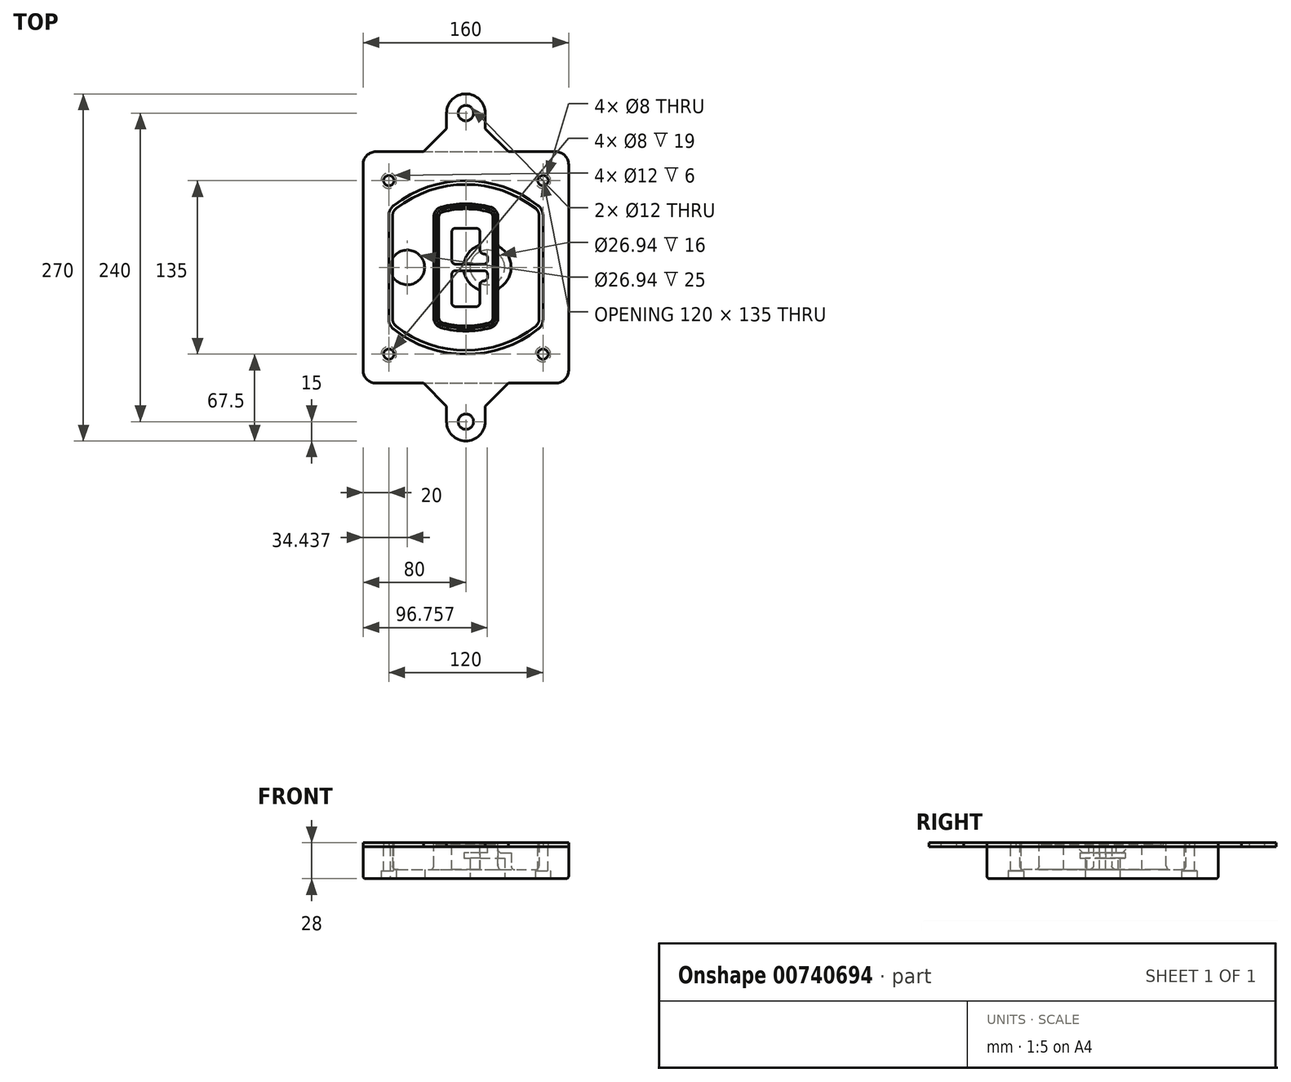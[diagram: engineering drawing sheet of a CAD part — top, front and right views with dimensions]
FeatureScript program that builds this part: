
annotation { "Feature Type Name" : "Feature", "Feature Type Description" : "" }
export const myFeature = defineFeature(function(context is Context, id is Id, definition is map)
    precondition{}
    {
        {
            var Q0;
            Q0=qCreatedBy(makeId("Top.planeOp"),FACE);
            var sketch = newSketch(context, id + "F0", { "sketchPlane" : qUnion([Q0])});
            skPoint(sketch, "E0.rect.middle", {"position": v(0, 0) * mm});
            skLineSegment(sketch, "E1.bottom", {"start": v(-70, -90) * mm, "end": v(70, -90) * mm});
            skLineSegment(sketch, "E1.top", {"start": v(-70, 90) * mm, "end": v(70, 90) * mm});
            skLineSegment(sketch, "E1.left", {"start": v(-80, -80) * mm, "end": v(-80, 80) * mm});
            skLineSegment(sketch, "E1.right", {"start": v(80, -80) * mm, "end": v(80, 80) * mm});
            skLineSegment(sketch, "E2", {"start": v(-80, 90) * mm, "end": v(80, -90) * mm, "construction": true});
            skLineSegment(sketch, "E3", {"start": v(80, 90) * mm, "end": v(-80, -90) * mm, "construction": true});
            skCircle(sketch, "E4", {"center": v(-60, 67.5) * mm, "radius": 4 * mm});
            skCircle(sketch, "E5", {"center": v(60, 67.5) * mm, "radius": 4 * mm});
            skCircle(sketch, "E6", {"center": v(60, -67.5) * mm, "radius": 4 * mm});
            skCircle(sketch, "E7", {"center": v(-60, -67.5) * mm, "radius": 4 * mm});
            skLineSegment(sketch, "E8", {"start": v(-60, 67.5) * mm, "end": v(60, 67.5) * mm, "construction": true});
            skLineSegment(sketch, "E9", {"start": v(60, 67.5) * mm, "end": v(60, -67.5) * mm, "construction": true});
            skLineSegment(sketch, "E10", {"start": v(60, -67.5) * mm, "end": v(-60, -67.5) * mm, "construction": true});
            skLineSegment(sketch, "E11", {"start": v(-60, -67.5) * mm, "end": v(-60, 67.5) * mm, "construction": true});
            skLineSegment(sketch, "E12", {"start": v(-60, 40.3) * mm, "end": v(-60, -40.3) * mm});
            skLineSegment(sketch, "E13", {"start": v(60, 40.3) * mm, "end": v(60, -40.3) * mm});
            skArc(sketch, "E14", {"start": v(56.15, 48.18) * mm, "mid": v(0, 67.5) * mm, "end": v(-56.15, 48.18) * mm});
            skArc(sketch, "E15", {"start": v(-56.15, -48.18) * mm, "mid": v(0, -67.5) * mm, "end": v(56.15, -48.18) * mm});
            skLineSegment(sketch, "E16", {"start": v(-60, 0) * mm, "end": v(60, 0) * mm, "construction": true});
            skPoint(sketch, "E17.visualSharp", {"position": v(-60, -45) * mm});
            skArc(sketch, "E17.filletArc", {"start": v(-60, -40.3) * mm, "mid": v(-58.99, -44.68) * mm, "end": v(-56.15, -48.18) * mm});
            skPoint(sketch, "E18.visualSharp", {"position": v(-60, 45) * mm});
            skArc(sketch, "E18.filletArc", {"start": v(-56.15, 48.18) * mm, "mid": v(-58.99, 44.68) * mm, "end": v(-60, 40.3) * mm});
            skPoint(sketch, "E19.visualSharp", {"position": v(60, 45) * mm});
            skArc(sketch, "E19.filletArc", {"start": v(60, 40.3) * mm, "mid": v(58.99, 44.68) * mm, "end": v(56.15, 48.18) * mm});
            skPoint(sketch, "E20.visualSharp", {"position": v(60, -45) * mm});
            skArc(sketch, "E20.filletArc", {"start": v(56.15, -48.18) * mm, "mid": v(58.99, -44.68) * mm, "end": v(60, -40.3) * mm});
            skPoint(sketch, "E21.visualSharp", {"position": v(-80, 90) * mm});
            skArc(sketch, "E21.filletArc", {"start": v(-70, 90) * mm, "mid": v(-77.07, 87.07) * mm, "end": v(-80, 80) * mm});
            skPoint(sketch, "E22.visualSharp", {"position": v(80, 90) * mm});
            skArc(sketch, "E22.filletArc", {"start": v(80, 80) * mm, "mid": v(77.07, 87.07) * mm, "end": v(70, 90) * mm});
            skPoint(sketch, "E23.visualSharp", {"position": v(80, -90) * mm});
            skArc(sketch, "E23.filletArc", {"start": v(70, -90) * mm, "mid": v(77.07, -87.07) * mm, "end": v(80, -80) * mm});
            skPoint(sketch, "E24.visualSharp", {"position": v(-80, -90) * mm});
            skArc(sketch, "E24.filletArc", {"start": v(-80, -80) * mm, "mid": v(-77.07, -87.07) * mm, "end": v(-70, -90) * mm});
            skArc(sketch, "E25.0", {"start": v(57, 40.3) * mm, "mid": v(56.3, 43.36) * mm, "end": v(54.3, 45.81) * mm});
            skLineSegment(sketch, "E25.1", {"start": v(57, 40.3) * mm, "end": v(57, -40.3) * mm});
            skArc(sketch, "E25.2", {"start": v(54.3, -45.81) * mm, "mid": v(56.3, -43.36) * mm, "end": v(57, -40.3) * mm});
            skArc(sketch, "E25.3", {"start": v(-54.3, -45.81) * mm, "mid": v(0, -64.5) * mm, "end": v(54.3, -45.81) * mm});
            skArc(sketch, "E25.4", {"start": v(-57, -40.3) * mm, "mid": v(-56.3, -43.36) * mm, "end": v(-54.3, -45.81) * mm});
            skArc(sketch, "E25.5", {"start": v(54.3, 45.81) * mm, "mid": v(0, 64.5) * mm, "end": v(-54.3, 45.81) * mm});
            skLineSegment(sketch, "E25.6", {"start": v(-57, 40.3) * mm, "end": v(-57, -40.3) * mm});
            skArc(sketch, "E25.7", {"start": v(-54.3, 45.81) * mm, "mid": v(-56.3, 43.36) * mm, "end": v(-57, 40.3) * mm});
            skArc(sketch, "E26.0", {"start": v(-58.62, 51.33) * mm, "mid": v(-62.58, 46.43) * mm, "end": v(-64, 40.3) * mm});
            skArc(sketch, "E26.1", {"start": v(58.62, 51.33) * mm, "mid": v(0, 71.5) * mm, "end": v(-58.62, 51.33) * mm});
            skArc(sketch, "E26.2", {"start": v(64, 40.3) * mm, "mid": v(62.58, 46.43) * mm, "end": v(58.62, 51.33) * mm});
            skLineSegment(sketch, "E26.3", {"start": v(64, 40.3) * mm, "end": v(64, -40.3) * mm});
            skArc(sketch, "E26.4", {"start": v(58.62, -51.33) * mm, "mid": v(62.58, -46.43) * mm, "end": v(64, -40.3) * mm});
            skLineSegment(sketch, "E26.5", {"start": v(-64, 40.3) * mm, "end": v(-64, -40.3) * mm});
            skArc(sketch, "E26.6", {"start": v(-58.62, -51.33) * mm, "mid": v(0, -71.5) * mm, "end": v(58.62, -51.33) * mm});
            skArc(sketch, "E26.7", {"start": v(-64, -40.3) * mm, "mid": v(-62.58, -46.43) * mm, "end": v(-58.62, -51.33) * mm});
            skSolve(sketch);
        }
        {
            var Q0;
            Q0=makeQuery(id+"F0.imprint","IMPRINT",FACE,{"disambiguationData":[TD([[makeQuery(id+"F0.imprint","IMPRINT",EDGE,{"derivedFrom":sQuery(id+"F0.wireOp",EDGE,"E1.bottom")}),1.0]])]});
            var Q1;
            Q1=makeQuery(id+"F0.imprint","IMPRINT",FACE,{"disambiguationData":[TD([[makeQuery(id+"F0.imprint","IMPRINT",EDGE,{"derivedFrom":sQuery(id+"F0.wireOp",EDGE,"E12")}),1.0]])]});
            var Q2;
            Q2=makeQuery(id+"F0.imprint","IMPRINT",FACE,{"disambiguationData":[TD([[makeQuery(id+"F0.imprint","IMPRINT",EDGE,{"derivedFrom":sQuery(id+"F0.wireOp",EDGE,"E25.0")}),1.0]])]});
            var Q3;
            Q3=makeQuery(id+"F0.imprint","IMPRINT",FACE,{"disambiguationData":[TD([[makeQuery(id+"F0.imprint","IMPRINT",EDGE,{"derivedFrom":sQuery(id+"F0.wireOp",EDGE,"E12")}),-1.0]])]});
            extrude(context, id + "F1", {"entities" : qUnion([Q0, Q1, Q2, Q3]), "oppositeDirection" : true, "depth" : 25 * mm});
        }
        {
            var Q0;
            Q0=makeQuery(id+"F0.imprint","IMPRINT",FACE,{"disambiguationData":[TD([[makeQuery(id+"F0.imprint","IMPRINT",EDGE,{"derivedFrom":sQuery(id+"F0.wireOp",EDGE,"E12")}),1.0]])]});
            extrude(context, id + "F2", {"entities" : qUnion([Q0]), "operationType" : NewBodyOperationType.ADD, "depth" : 3 * mm});
        }
        {
            var Q0;
            Q0=makeQuery(id+"F0.imprint","IMPRINT",FACE,{"disambiguationData":[TD([[makeQuery(id+"F0.imprint","IMPRINT",EDGE,{"derivedFrom":sQuery(id+"F0.wireOp",EDGE,"E25.0")}),1.0]])]});
            extrude(context, id + "F3", {"entities" : qUnion([Q0]), "operationType" : NewBodyOperationType.REMOVE, "oppositeDirection" : true, "depth" : 18 * mm});
        }
        {
            var Q0;
            Q0=makeQuery(id+"F2.opExtrude","CAP_FACE",FACE,{"disambiguationData":[OSD([sQuery(id+"F0.wireOp",EDGE,"E12"),sQuery(id+"F0.wireOp",EDGE,"E13"),sQuery(id+"F0.wireOp",EDGE,"E14"),sQuery(id+"F0.wireOp",EDGE,"E15"),sQuery(id+"F0.wireOp",EDGE,"E17.filletArc"),sQuery(id+"F0.wireOp",EDGE,"E18.filletArc"),sQuery(id+"F0.wireOp",EDGE,"E19.filletArc"),sQuery(id+"F0.wireOp",EDGE,"E20.filletArc"),sQuery(id+"F0.wireOp",EDGE,"E25.0"),sQuery(id+"F0.wireOp",EDGE,"E25.1"),sQuery(id+"F0.wireOp",EDGE,"E25.2"),sQuery(id+"F0.wireOp",EDGE,"E25.3"),sQuery(id+"F0.wireOp",EDGE,"E25.4"),sQuery(id+"F0.wireOp",EDGE,"E25.5"),sQuery(id+"F0.wireOp",EDGE,"E25.6"),sQuery(id+"F0.wireOp",EDGE,"E25.7")])],"isStart":false});
            var sketch = newSketch(context, id + "F4", { "sketchPlane" : qUnion([Q0])});
            skArc(sketch, "E27.0", {"start": v(-19.08, -46.97) * mm, "mid": v(0, -49.5) * mm, "end": v(19.08, -46.97) * mm});
            skArc(sketch, "E28.0", {"start": v(19.08, 46.97) * mm, "mid": v(0, 49.5) * mm, "end": v(-19.08, 46.97) * mm});
            skLineSegment(sketch, "E29", {"start": v(-25, 39.25) * mm, "end": v(-25, -39.25) * mm});
            skLineSegment(sketch, "E30", {"start": v(25, 39.25) * mm, "end": v(25, -39.25) * mm});
            skLineSegment(sketch, "E31", {"start": v(-25, 45.1) * mm, "end": v(25, 45.1) * mm, "construction": true});
            skLineSegment(sketch, "E32", {"start": v(-25, -45.1) * mm, "end": v(25, -45.1) * mm, "construction": true});
            skPoint(sketch, "E33.visualSharp", {"position": v(-25, 45.1) * mm});
            skArc(sketch, "E33.filletArc", {"start": v(-19.08, 46.97) * mm, "mid": v(-23.35, 44.11) * mm, "end": v(-25, 39.25) * mm});
            skPoint(sketch, "E34.visualSharp", {"position": v(25, 45.1) * mm});
            skArc(sketch, "E34.filletArc", {"start": v(25, 39.25) * mm, "mid": v(23.35, 44.11) * mm, "end": v(19.08, 46.97) * mm});
            skPoint(sketch, "E35.visualSharp", {"position": v(25, -45.1) * mm});
            skArc(sketch, "E35.filletArc", {"start": v(19.08, -46.97) * mm, "mid": v(23.35, -44.11) * mm, "end": v(25, -39.25) * mm});
            skPoint(sketch, "E36.visualSharp", {"position": v(-25, -45.1) * mm});
            skArc(sketch, "E36.filletArc", {"start": v(-25, -39.25) * mm, "mid": v(-23.35, -44.11) * mm, "end": v(-19.08, -46.97) * mm});
            skArc(sketch, "E37.0", {"start": v(54.3, 45.81) * mm, "mid": v(0, 64.5) * mm, "end": v(-54.3, 45.81) * mm});
            skArc(sketch, "E37.1", {"start": v(-54.3, 45.81) * mm, "mid": v(-56.3, 43.36) * mm, "end": v(-57, 40.3) * mm});
            skLineSegment(sketch, "E37.2", {"start": v(-57, 40.3) * mm, "end": v(-57, -40.3) * mm});
            skArc(sketch, "E37.3", {"start": v(-57, -40.3) * mm, "mid": v(-56.3, -43.36) * mm, "end": v(-54.3, -45.81) * mm});
            skArc(sketch, "E37.4", {"start": v(-54.3, -45.81) * mm, "mid": v(0, -64.5) * mm, "end": v(54.3, -45.81) * mm});
            skArc(sketch, "E37.5", {"start": v(54.3, -45.81) * mm, "mid": v(56.3, -43.36) * mm, "end": v(57, -40.3) * mm});
            skLineSegment(sketch, "E37.6", {"start": v(57, 40.3) * mm, "end": v(57, -40.3) * mm});
            skArc(sketch, "E37.7", {"start": v(57, 40.3) * mm, "mid": v(56.3, 43.36) * mm, "end": v(54.3, 45.81) * mm});
            skLineSegment(sketch, "E38.0", {"start": v(23, 39.25) * mm, "end": v(23, -39.25) * mm});
            skArc(sketch, "E38.1", {"start": v(18.56, -45.04) * mm, "mid": v(21.76, -42.9) * mm, "end": v(23, -39.25) * mm});
            skArc(sketch, "E38.2", {"start": v(-18.56, -45.04) * mm, "mid": v(0, -47.5) * mm, "end": v(18.56, -45.04) * mm});
            skArc(sketch, "E38.3", {"start": v(-23, -39.25) * mm, "mid": v(-21.76, -42.9) * mm, "end": v(-18.56, -45.04) * mm});
            skLineSegment(sketch, "E38.4", {"start": v(-23, 39.25) * mm, "end": v(-23, -39.25) * mm});
            skArc(sketch, "E38.5", {"start": v(23, 39.25) * mm, "mid": v(21.76, 42.9) * mm, "end": v(18.56, 45.04) * mm});
            skArc(sketch, "E38.6", {"start": v(-18.56, 45.04) * mm, "mid": v(-21.76, 42.9) * mm, "end": v(-23, 39.25) * mm});
            skArc(sketch, "E38.7", {"start": v(18.56, 45.04) * mm, "mid": v(0, 47.5) * mm, "end": v(-18.56, 45.04) * mm});
            skArc(sketch, "E39.0", {"start": v(21, 39.25) * mm, "mid": v(20.18, 41.68) * mm, "end": v(18.04, 43.1) * mm});
            skLineSegment(sketch, "E39.1", {"start": v(21, 39.25) * mm, "end": v(21, -39.25) * mm});
            skArc(sketch, "E39.2", {"start": v(18.04, -43.1) * mm, "mid": v(20.18, -41.68) * mm, "end": v(21, -39.25) * mm});
            skArc(sketch, "E39.3", {"start": v(-18.04, -43.1) * mm, "mid": v(0, -45.5) * mm, "end": v(18.04, -43.1) * mm});
            skArc(sketch, "E39.4", {"start": v(-21, -39.25) * mm, "mid": v(-20.18, -41.68) * mm, "end": v(-18.04, -43.1) * mm});
            skArc(sketch, "E39.5", {"start": v(18.04, 43.1) * mm, "mid": v(0, 45.5) * mm, "end": v(-18.04, 43.1) * mm});
            skLineSegment(sketch, "E39.6", {"start": v(-21, 39.25) * mm, "end": v(-21, -39.25) * mm});
            skArc(sketch, "E39.7", {"start": v(-18.04, 43.1) * mm, "mid": v(-20.18, 41.68) * mm, "end": v(-21, 39.25) * mm});
            skLineSegment(sketch, "E40", {"start": v(-25, 0) * mm, "end": v(25, 0) * mm, "construction": true});
            skLineSegment(sketch, "E41", {"start": v(-11, 5.5) * mm, "end": v(-11, 27.5) * mm});
            skLineSegment(sketch, "E42", {"start": v(-8, 30.5) * mm, "end": v(8, 30.5) * mm});
            skLineSegment(sketch, "E43", {"start": v(11, 27.5) * mm, "end": v(11, 13.5) * mm});
            skLineSegment(sketch, "E44", {"start": v(14, 10.5) * mm, "end": v(14, 10.5) * mm});
            skLineSegment(sketch, "E45", {"start": v(17, 7.5) * mm, "end": v(17, 5.5) * mm});
            skLineSegment(sketch, "E46", {"start": v(14, 2.5) * mm, "end": v(-8, 2.5) * mm});
            skPoint(sketch, "E47.visualSharp", {"position": v(-11, 30.5) * mm});
            skArc(sketch, "E47.filletArc", {"start": v(-8, 30.5) * mm, "mid": v(-10.12, 29.62) * mm, "end": v(-11, 27.5) * mm});
            skPoint(sketch, "E48.visualSharp", {"position": v(11, 30.5) * mm});
            skArc(sketch, "E48.filletArc", {"start": v(11, 27.5) * mm, "mid": v(10.12, 29.62) * mm, "end": v(8, 30.5) * mm});
            skPoint(sketch, "E49.visualSharp", {"position": v(11, 10.5) * mm});
            skArc(sketch, "E49.filletArc", {"start": v(11, 13.5) * mm, "mid": v(11.88, 11.38) * mm, "end": v(14, 10.5) * mm});
            skPoint(sketch, "E50.visualSharp", {"position": v(17, 10.5) * mm});
            skArc(sketch, "E50.filletArc", {"start": v(17, 7.5) * mm, "mid": v(16.12, 9.62) * mm, "end": v(14, 10.5) * mm});
            skPoint(sketch, "E51.visualSharp", {"position": v(17, 2.5) * mm});
            skArc(sketch, "E51.filletArc", {"start": v(14, 2.5) * mm, "mid": v(16.12, 3.38) * mm, "end": v(17, 5.5) * mm});
            skPoint(sketch, "E52.visualSharp", {"position": v(-11, 2.5) * mm});
            skArc(sketch, "E52.filletArc", {"start": v(-11, 5.5) * mm, "mid": v(-10.12, 3.38) * mm, "end": v(-8, 2.5) * mm});
            skLineSegment(sketch, "E53.0.MirrorCS", {"start": v(14, -2.5) * mm, "end": v(-8, -2.5) * mm});
            skArc(sketch, "E54.0.MirrorCS", {"start": v(-11, -5.5) * mm, "mid": v(-10.12, -3.38) * mm, "end": v(-8, -2.5) * mm});
            skLineSegment(sketch, "E55.0.MirrorCS", {"start": v(-11, -5.5) * mm, "end": v(-11, -27.5) * mm});
            skArc(sketch, "E56.0.MirrorCS", {"start": v(-8, -30.5) * mm, "mid": v(-10.12, -29.62) * mm, "end": v(-11, -27.5) * mm});
            skLineSegment(sketch, "E57.0.MirrorCS", {"start": v(-8, -30.5) * mm, "end": v(8, -30.5) * mm});
            skArc(sketch, "E58.0.MirrorCS", {"start": v(11, -27.5) * mm, "mid": v(10.12, -29.62) * mm, "end": v(8, -30.5) * mm});
            skLineSegment(sketch, "E59.0.MirrorCS", {"start": v(11, -27.5) * mm, "end": v(11, -13.5) * mm});
            skArc(sketch, "E60.0.MirrorCS", {"start": v(11, -13.5) * mm, "mid": v(11.88, -11.38) * mm, "end": v(14, -10.5) * mm});
            skArc(sketch, "E61.0.MirrorCS", {"start": v(17, -7.5) * mm, "mid": v(16.12, -9.62) * mm, "end": v(14, -10.5) * mm});
            skLineSegment(sketch, "E62.0.MirrorCS", {"start": v(17, -7.5) * mm, "end": v(17, -5.5) * mm});
            skArc(sketch, "E63.0.MirrorCS", {"start": v(14, -2.5) * mm, "mid": v(16.12, -3.38) * mm, "end": v(17, -5.5) * mm});
            skSolve(sketch);
        }
        {
            var Q0;
            Q0=makeQuery(id+"F4.imprint","IMPRINT",FACE,{"disambiguationData":[TD([[makeQuery(id+"F4.imprint","IMPRINT",EDGE,{"derivedFrom":sQuery(id+"F4.wireOp",EDGE,"E27.0")}),1.0]])]});
            var Q1;
            Q1=makeQuery(id+"F4.imprint","IMPRINT",FACE,{"disambiguationData":[TD([[makeQuery(id+"F4.imprint","IMPRINT",EDGE,{"derivedFrom":sQuery(id+"F4.wireOp",EDGE,"E38.0")}),-1.0]])]});
            var Q2;
            Q2=makeQuery(id+"F4.imprint","IMPRINT",FACE,{"disambiguationData":[TD([[makeQuery(id+"F4.imprint","IMPRINT",EDGE,{"derivedFrom":sQuery(id+"F4.wireOp",EDGE,"E39.0")}),1.0]])]});
            extrude(context, id + "F5", {"entities" : qUnion([Q0, Q1, Q2]), "operationType" : NewBodyOperationType.ADD, "endBound" : BoundingType.UP_TO_NEXT, "oppositeDirection" : true, "depth" : 25 * mm});
        }
        {
            var Q0;
            Q0=makeQuery(id+"F4.imprint","IMPRINT",FACE,{"disambiguationData":[TD([[makeQuery(id+"F4.imprint","IMPRINT",EDGE,{"derivedFrom":sQuery(id+"F4.wireOp",EDGE,"E38.0")}),-1.0]])]});
            extrude(context, id + "F6", {"entities" : qUnion([Q0]), "operationType" : NewBodyOperationType.REMOVE, "oppositeDirection" : true, "depth" : 2 * mm});
        }
        {
            var Q0;
            Q0=makeQuery(id+"F1.opExtrude","CAP_FACE",FACE,{"disambiguationData":[OSD([sQuery(id+"F0.wireOp",EDGE,"E1.bottom"),sQuery(id+"F0.wireOp",EDGE,"E1.top"),sQuery(id+"F0.wireOp",EDGE,"E1.left"),sQuery(id+"F0.wireOp",EDGE,"E1.right"),sQuery(id+"F0.wireOp",EDGE,"E4"),sQuery(id+"F0.wireOp",EDGE,"E5"),sQuery(id+"F0.wireOp",EDGE,"E6"),sQuery(id+"F0.wireOp",EDGE,"E7"),sQuery(id+"F0.wireOp",EDGE,"E21.filletArc"),sQuery(id+"F0.wireOp",EDGE,"E22.filletArc"),sQuery(id+"F0.wireOp",EDGE,"E23.filletArc"),sQuery(id+"F0.wireOp",EDGE,"E24.filletArc")])],"isStart":false});
            var sketch = newSketch(context, id + "F7", { "sketchPlane" : qUnion([Q0])});
            skCircle(sketch, "E64", {"center": v(16.76, 0) * mm, "radius": 13.47 * mm});
            skCircle(sketch, "E65", {"center": v(-45.56, 0) * mm, "radius": 13.47 * mm});
            skLineSegment(sketch, "E66", {"start": v(80, 0) * mm, "end": v(-80, 0) * mm});
            skCircle(sketch, "E67", {"center": v(16.76, 0) * mm, "radius": 18.47 * mm});
            skCircle(sketch, "E68", {"center": v(60, -67.5) * mm, "radius": 6 * mm});
            skCircle(sketch, "E69", {"center": v(-60, -67.5) * mm, "radius": 6 * mm});
            skCircle(sketch, "E70", {"center": v(-60, 67.5) * mm, "radius": 6 * mm});
            skCircle(sketch, "E71", {"center": v(60, 67.5) * mm, "radius": 6 * mm});
            skSolve(sketch);
        }
        {
            var Q0;
            {var subQ1=sQuery(id+"F7.wireOp",EDGE,"E66");var subQ4=sQuery(id+"F7.wireOp",EDGE,"E64");var subQ6=makeQuery(id+"F7.imprint","INTERSECT",VERTEX,{"disambiguationData":[OD(0.0)],"derivedFrom":[subQ4,subQ1]});Q0=makeQuery(id+"F7.imprint","IMPRINT",FACE,{"disambiguationData":[TD([[makeQuery(id+"F7.imprint","IMPRINT",EDGE,{"disambiguationData":[TD([[subQ6,-1.0]])],"derivedFrom":subQ4}),-1.0]])]});}
            var Q1;
            {var subQ0=sQuery(id+"F7.wireOp",EDGE,"E66");var subQ1=sQuery(id+"F7.wireOp",EDGE,"E64");var subQ3=makeQuery(id+"F7.imprint","INTERSECT",VERTEX,{"disambiguationData":[OD(0.0)],"derivedFrom":[subQ1,subQ0]});Q1=makeQuery(id+"F7.imprint","IMPRINT",FACE,{"disambiguationData":[TD([[makeQuery(id+"F7.imprint","IMPRINT",EDGE,{"disambiguationData":[TD([[subQ3,-1.0]])],"derivedFrom":subQ1}),1.0]])]});}
            var Q2;
            {var subQ0=sQuery(id+"F7.wireOp",EDGE,"E66");var subQ1=sQuery(id+"F7.wireOp",EDGE,"E64");var subQ3=makeQuery(id+"F7.imprint","INTERSECT",VERTEX,{"disambiguationData":[OD(0.0)],"derivedFrom":[subQ1,subQ0]});Q2=makeQuery(id+"F7.imprint","IMPRINT",FACE,{"disambiguationData":[TD([[makeQuery(id+"F7.imprint","IMPRINT",EDGE,{"disambiguationData":[TD([[subQ3,1.0]])],"derivedFrom":subQ1}),1.0]])]});}
            var Q3;
            {var subQ1=sQuery(id+"F7.wireOp",EDGE,"E66");var subQ4=sQuery(id+"F7.wireOp",EDGE,"E64");var subQ6=makeQuery(id+"F7.imprint","INTERSECT",VERTEX,{"disambiguationData":[OD(0.0)],"derivedFrom":[subQ4,subQ1]});Q3=makeQuery(id+"F7.imprint","IMPRINT",FACE,{"disambiguationData":[TD([[makeQuery(id+"F7.imprint","IMPRINT",EDGE,{"disambiguationData":[TD([[subQ6,1.0]])],"derivedFrom":subQ4}),-1.0]])]});}
            extrude(context, id + "F8", {"entities" : qUnion([Q0, Q1, Q2, Q3]), "operationType" : NewBodyOperationType.ADD, "oppositeDirection" : true, "depth" : 20 * mm});
        }
        {
            var Q0;
            {var subQ0=sQuery(id+"F7.wireOp",EDGE,"E66");var subQ1=sQuery(id+"F7.wireOp",EDGE,"E64");var subQ3=makeQuery(id+"F7.imprint","INTERSECT",VERTEX,{"disambiguationData":[OD(0.0)],"derivedFrom":[subQ1,subQ0]});Q0=makeQuery(id+"F7.imprint","IMPRINT",FACE,{"disambiguationData":[TD([[makeQuery(id+"F7.imprint","IMPRINT",EDGE,{"disambiguationData":[TD([[subQ3,-1.0]])],"derivedFrom":subQ1}),1.0]])]});}
            var Q1;
            {var subQ0=sQuery(id+"F7.wireOp",EDGE,"E66");var subQ1=sQuery(id+"F7.wireOp",EDGE,"E64");var subQ3=makeQuery(id+"F7.imprint","INTERSECT",VERTEX,{"disambiguationData":[OD(0.0)],"derivedFrom":[subQ1,subQ0]});Q1=makeQuery(id+"F7.imprint","IMPRINT",FACE,{"disambiguationData":[TD([[makeQuery(id+"F7.imprint","IMPRINT",EDGE,{"disambiguationData":[TD([[subQ3,1.0]])],"derivedFrom":subQ1}),1.0]])]});}
            extrude(context, id + "F9", {"entities" : qUnion([Q0, Q1]), "operationType" : NewBodyOperationType.REMOVE, "oppositeDirection" : true, "depth" : 16 * mm});
        }
        {
            var Q0;
            {var subQ0=sQuery(id+"F7.wireOp",EDGE,"E66");var subQ1=sQuery(id+"F7.wireOp",EDGE,"E65");var subQ3=makeQuery(id+"F7.imprint","INTERSECT",VERTEX,{"disambiguationData":[OD(0.0)],"derivedFrom":[subQ1,subQ0]});Q0=makeQuery(id+"F7.imprint","IMPRINT",FACE,{"disambiguationData":[TD([[makeQuery(id+"F7.imprint","IMPRINT",EDGE,{"disambiguationData":[TD([[subQ3,-1.0]])],"derivedFrom":subQ1}),1.0]])]});}
            var Q1;
            {var subQ0=sQuery(id+"F7.wireOp",EDGE,"E66");var subQ1=sQuery(id+"F7.wireOp",EDGE,"E65");var subQ3=makeQuery(id+"F7.imprint","INTERSECT",VERTEX,{"disambiguationData":[OD(0.0)],"derivedFrom":[subQ1,subQ0]});Q1=makeQuery(id+"F7.imprint","IMPRINT",FACE,{"disambiguationData":[TD([[makeQuery(id+"F7.imprint","IMPRINT",EDGE,{"disambiguationData":[TD([[subQ3,1.0]])],"derivedFrom":subQ1}),1.0]])]});}
            extrude(context, id + "F10", {"entities" : qUnion([Q0, Q1]), "operationType" : NewBodyOperationType.REMOVE, "oppositeDirection" : true, "depth" : 25 * mm});
        }
        {
            var Q0;
            Q0=makeQuery(id+"F7.imprint","IMPRINT",FACE,{"disambiguationData":[TD([[makeQuery(id+"F7.imprint","IMPRINT",EDGE,{"derivedFrom":sQuery(id+"F7.wireOp",EDGE,"E68")}),1.0]])]});
            var Q1;
            Q1=makeQuery(id+"F7.imprint","IMPRINT",FACE,{"disambiguationData":[TD([[makeQuery(id+"F7.imprint","IMPRINT",EDGE,{"derivedFrom":makeQuery(id+"F1.opExtrude","CAP_EDGE",EDGE,{"disambiguationData":[OSD([sQuery(id+"F0.wireOp",EDGE,"E5")])],"isStart":false})}),-1.0]])]});
            var Q2;
            Q2=makeQuery(id+"F7.imprint","IMPRINT",FACE,{"disambiguationData":[TD([[makeQuery(id+"F7.imprint","IMPRINT",EDGE,{"derivedFrom":sQuery(id+"F7.wireOp",EDGE,"E69")}),1.0]])]});
            var Q3;
            Q3=makeQuery(id+"F7.imprint","IMPRINT",FACE,{"disambiguationData":[TD([[makeQuery(id+"F7.imprint","IMPRINT",EDGE,{"derivedFrom":makeQuery(id+"F1.opExtrude","CAP_EDGE",EDGE,{"disambiguationData":[OSD([sQuery(id+"F0.wireOp",EDGE,"E4")])],"isStart":false})}),-1.0]])]});
            var Q4;
            Q4=makeQuery(id+"F7.imprint","IMPRINT",FACE,{"disambiguationData":[TD([[makeQuery(id+"F7.imprint","IMPRINT",EDGE,{"derivedFrom":sQuery(id+"F7.wireOp",EDGE,"E70")}),1.0]])]});
            var Q5;
            Q5=makeQuery(id+"F7.imprint","IMPRINT",FACE,{"disambiguationData":[TD([[makeQuery(id+"F7.imprint","IMPRINT",EDGE,{"derivedFrom":makeQuery(id+"F1.opExtrude","CAP_EDGE",EDGE,{"disambiguationData":[OSD([sQuery(id+"F0.wireOp",EDGE,"E7")])],"isStart":false})}),-1.0]])]});
            var Q6;
            Q6=makeQuery(id+"F7.imprint","IMPRINT",FACE,{"disambiguationData":[TD([[makeQuery(id+"F7.imprint","IMPRINT",EDGE,{"derivedFrom":sQuery(id+"F7.wireOp",EDGE,"E71")}),1.0]])]});
            var Q7;
            Q7=makeQuery(id+"F7.imprint","IMPRINT",FACE,{"disambiguationData":[TD([[makeQuery(id+"F7.imprint","IMPRINT",EDGE,{"derivedFrom":makeQuery(id+"F1.opExtrude","CAP_EDGE",EDGE,{"disambiguationData":[OSD([sQuery(id+"F0.wireOp",EDGE,"E6")])],"isStart":false})}),-1.0]])]});
            extrude(context, id + "F11", {"entities" : qUnion([Q0, Q1, Q2, Q3, Q4, Q5, Q6, Q7]), "operationType" : NewBodyOperationType.REMOVE, "oppositeDirection" : true, "depth" : 6 * mm});
        }
        {
            var Q0;
            Q0=makeQuery(id+"F9.boolean.opBoolean","COPY",FACE,{"derivedFrom":makeQuery(id+"F9.opExtrude","CAP_FACE",FACE,{"disambiguationData":[OSD([sQuery(id+"F7.wireOp",EDGE,"E64")])],"isStart":false})});
            var sketch = newSketch(context, id + "F12", { "sketchPlane" : qUnion([Q0])});
            skArc(sketch, "E72.0", {"start": v(11, 17.55) * mm, "mid": v(2.57, 11.82) * mm, "end": v(-1.54, 2.5) * mm});
            skArc(sketch, "E72.1", {"start": v(-1.54, -2.5) * mm, "mid": v(2.57, -11.82) * mm, "end": v(11, -17.55) * mm});
            skLineSegment(sketch, "E73", {"start": v(-1.54, -2.5) * mm, "end": v(14, -2.5) * mm});
            skLineSegment(sketch, "E74.0", {"start": v(14, 2.5) * mm, "end": v(-1.54, 2.5) * mm});
            skArc(sketch, "E74.1", {"start": v(14, 2.5) * mm, "mid": v(16.12, 3.38) * mm, "end": v(17, 5.5) * mm});
            skLineSegment(sketch, "E74.2", {"start": v(17, 7.5) * mm, "end": v(17, 5.5) * mm});
            skArc(sketch, "E74.3", {"start": v(17, 7.5) * mm, "mid": v(16.12, 9.62) * mm, "end": v(14, 10.5) * mm});
            skArc(sketch, "E74.4", {"start": v(11, 13.5) * mm, "mid": v(11.88, 11.38) * mm, "end": v(14, 10.5) * mm});
            skLineSegment(sketch, "E74.5", {"start": v(11, 17.55) * mm, "end": v(11, 13.5) * mm});
            skLineSegment(sketch, "E74.7", {"start": v(14, -2.5) * mm, "end": v(-1.54, -2.5) * mm});
            skArc(sketch, "E74.8", {"start": v(14, -2.5) * mm, "mid": v(16.12, -3.38) * mm, "end": v(17, -5.5) * mm});
            skLineSegment(sketch, "E74.9", {"start": v(17, -7.5) * mm, "end": v(17, -5.5) * mm});
            skArc(sketch, "E74.10", {"start": v(17, -7.5) * mm, "mid": v(16.12, -9.62) * mm, "end": v(14, -10.5) * mm});
            skArc(sketch, "E74.11", {"start": v(11, -13.5) * mm, "mid": v(11.88, -11.38) * mm, "end": v(14, -10.5) * mm});
            skLineSegment(sketch, "E74.12", {"start": v(11, -17.55) * mm, "end": v(11, -13.5) * mm});
            skPoint(sketch, "E75.orphan", {"position": v(11, -27.5) * mm});
            skPoint(sketch, "E76.orphan", {"position": v(-8, -2.5) * mm});
            skPoint(sketch, "E77.orphan", {"position": v(-8, 2.5) * mm});
            skPoint(sketch, "E78.orphan", {"position": v(11, 27.5) * mm});
            skSolve(sketch);
        }
        {
            var Q0;
            {var subQ7=sQuery(id+"F12.wireOp",EDGE,"E72.0");var subQ14=sQuery(id+"F12.wireOp",EDGE,"E72.1");var subQ16=sQuery(id+"F12.wireOp",EDGE,"E74.1");var subQ18=sQuery(id+"F12.wireOp",EDGE,"E74.8");Q0=qUnion([makeQuery(id+"F12.imprint","IMPRINT",FACE,{"disambiguationData":[TD([[makeQuery(id+"F12.imprint","IMPRINT",EDGE,{"derivedFrom":subQ7}),1.0]])]}),makeQuery(id+"F12.imprint","IMPRINT",FACE,{"disambiguationData":[TD([[makeQuery(id+"F12.imprint","IMPRINT",EDGE,{"derivedFrom":subQ14}),1.0]])]}),makeQuery(id+"F12.imprint","IMPRINT",FACE,{"disambiguationData":[TD([[makeQuery(id+"F12.imprint","IMPRINT",EDGE,{"derivedFrom":subQ16}),1.0]])]}),makeQuery(id+"F12.imprint","IMPRINT",FACE,{"disambiguationData":[TD([[makeQuery(id+"F12.imprint","IMPRINT",EDGE,{"derivedFrom":subQ18}),-1.0]])]})]);}
            var Q1;
            Q1=makeQuery(id+"F5.boolean.opBoolean","SPLIT",FACE,{"disambiguationData":[TD([makeQuery(id+"F5.opExtrude","SWEPT_FACE",FACE,{"disambiguationData":[OSD([sQuery(id+"F4.wireOp",EDGE,"E41")])]})])],"derivedFrom":makeQuery(id+"F3.boolean.opBoolean","COPY",FACE,{"derivedFrom":makeQuery(id+"F3.opExtrude","CAP_FACE",FACE,{"disambiguationData":[OSD([sQuery(id+"F0.wireOp",EDGE,"E25.0"),sQuery(id+"F0.wireOp",EDGE,"E25.1"),sQuery(id+"F0.wireOp",EDGE,"E25.2"),sQuery(id+"F0.wireOp",EDGE,"E25.3"),sQuery(id+"F0.wireOp",EDGE,"E25.4"),sQuery(id+"F0.wireOp",EDGE,"E25.5"),sQuery(id+"F0.wireOp",EDGE,"E25.6"),sQuery(id+"F0.wireOp",EDGE,"E25.7")])],"isStart":false})})});
            extrude(context, id + "F13", {"entities" : qUnion([Q0]), "operationType" : NewBodyOperationType.REMOVE, "endBound" : BoundingType.UP_TO_SURFACE, "endBoundEntityFace" : qUnion([Q1]), "depth" : 25 * mm});
        }
        {
            var Q0;
            Q0=makeQuery(id+"F3.boolean.opBoolean","COPY",EDGE,{"derivedFrom":makeQuery(id+"F3.opExtrude","CAP_EDGE",EDGE,{"disambiguationData":[OSD([sQuery(id+"F0.wireOp",EDGE,"E25.6")])],"isStart":false})});
            var Q1;
            Q1=makeQuery(id+"F8.boolean.opBoolean","INTERSECT",EDGE,{"derivedFrom":[makeQuery(id+"F5.opExtrude","SWEPT_FACE",FACE,{"disambiguationData":[OSD([sQuery(id+"F4.wireOp",EDGE,"E30")])]}),makeQuery(id+"F8.opExtrude","CAP_FACE",FACE,{"disambiguationData":[OSD([sQuery(id+"F7.wireOp",EDGE,"E67")])],"isStart":false})]});
            var Q2;
            Q2=makeQuery(id+"F8.boolean.opBoolean","INTERSECT",EDGE,{"disambiguationData":[OD(1.0)],"derivedFrom":[makeQuery(id+"F5.opExtrude","SWEPT_FACE",FACE,{"disambiguationData":[OSD([sQuery(id+"F4.wireOp",EDGE,"E30")])]}),makeQuery(id+"F8.opExtrude","SWEPT_FACE",FACE,{"disambiguationData":[OSD([sQuery(id+"F7.wireOp",EDGE,"E67")])]})]});
            var Q3;
            {var subQ0=sQuery(id+"F4.wireOp",EDGE,"E30");Q3=makeQuery(id+"F8.boolean.opBoolean","SPLIT",EDGE,{"disambiguationData":[TD([makeQuery(id+"F5.opExtrude","SWEPT_FACE",FACE,{"disambiguationData":[OSD([sQuery(id+"F4.wireOp",EDGE,"E35.filletArc")])]})])],"derivedFrom":makeQuery(id+"F5.opExtrude","CAP_EDGE",EDGE,{"disambiguationData":[OSD([subQ0])],"isStart":false})});}
            var Q4;
            {var subQ0=sQuery(id+"F0.wireOp",EDGE,"E25.7");var subQ1=sQuery(id+"F0.wireOp",EDGE,"E25.1");var subQ2=sQuery(id+"F0.wireOp",EDGE,"E25.6");var subQ3=sQuery(id+"F0.wireOp",EDGE,"E25.5");var subQ4=sQuery(id+"F0.wireOp",EDGE,"E25.4");var subQ5=sQuery(id+"F0.wireOp",EDGE,"E25.0");var subQ6=sQuery(id+"F0.wireOp",EDGE,"E25.2");var subQ7=sQuery(id+"F0.wireOp",EDGE,"E25.3");Q4=makeQuery(id+"F8.boolean.opBoolean","INTERSECT",EDGE,{"derivedFrom":[makeQuery(id+"F5.boolean.opBoolean","SPLIT",FACE,{"disambiguationData":[TD([makeQuery(id+"F2.opExtrude","SWEPT_FACE",FACE,{"disambiguationData":[OSD([subQ5])]})])],"derivedFrom":makeQuery(id+"F3.boolean.opBoolean","COPY",FACE,{"derivedFrom":makeQuery(id+"F3.opExtrude","CAP_FACE",FACE,{"disambiguationData":[OSD([subQ5,subQ1,subQ6,subQ7,subQ4,subQ3,subQ2,subQ0])],"isStart":false})})}),makeQuery(id+"F8.opExtrude","SWEPT_FACE",FACE,{"disambiguationData":[OSD([sQuery(id+"F7.wireOp",EDGE,"E67")])]})]});}
            var Q5;
            Q5=makeQuery(id+"F8.boolean.opBoolean","INTERSECT",EDGE,{"disambiguationData":[OD(0.0)],"derivedFrom":[makeQuery(id+"F5.opExtrude","SWEPT_FACE",FACE,{"disambiguationData":[OSD([sQuery(id+"F4.wireOp",EDGE,"E30")])]}),makeQuery(id+"F8.opExtrude","SWEPT_FACE",FACE,{"disambiguationData":[OSD([sQuery(id+"F7.wireOp",EDGE,"E67")])]})]});
            fillet(context, id + "F14", {"entities" : qUnion([Q0, Q1, Q2, Q3, Q4, Q5]), "radius" : 3 * mm, "tangentPropagation" : true, "allowEdgeOverflow" : false});
        }
        {
            var Q0;
            Q0=makeQuery(id+"F1.opExtrude","CAP_EDGE",EDGE,{"disambiguationData":[OSD([sQuery(id+"F0.wireOp",EDGE,"E1.bottom")])],"isStart":false});
            fillet(context, id + "F15", {"entities" : qUnion([Q0]), "radius" : 2 * mm, "tangentPropagation" : true, "allowEdgeOverflow" : false});
        }
        {
            var Q0;
            {var subQ0=sQuery(id+"F0.wireOp",EDGE,"E21.filletArc");var subQ1=sQuery(id+"F0.wireOp",EDGE,"E7");var subQ2=sQuery(id+"F0.wireOp",EDGE,"E6");var subQ3=sQuery(id+"F0.wireOp",EDGE,"E5");var subQ4=sQuery(id+"F0.wireOp",EDGE,"E4");var subQ5=sQuery(id+"F0.wireOp",EDGE,"E22.filletArc");var subQ6=sQuery(id+"F0.wireOp",EDGE,"E1.bottom");var subQ7=sQuery(id+"F0.wireOp",EDGE,"E1.right");var subQ8=sQuery(id+"F0.wireOp",EDGE,"E1.top");var subQ9=sQuery(id+"F0.wireOp",EDGE,"E1.left");var subQ10=sQuery(id+"F0.wireOp",EDGE,"E23.filletArc");var subQ11=sQuery(id+"F0.wireOp",EDGE,"E24.filletArc");Q0=makeQuery(id+"F2.boolean.opBoolean","SPLIT",FACE,{"disambiguationData":[TD([makeQuery(id+"F1.opExtrude","SWEPT_FACE",FACE,{"disambiguationData":[OSD([subQ6])]})])],"derivedFrom":makeQuery(id+"F1.opExtrude","CAP_FACE",FACE,{"disambiguationData":[OSD([subQ6,subQ8,subQ9,subQ7,subQ4,subQ3,subQ2,subQ1,subQ0,subQ5,subQ10,subQ11])],"isStart":true})});}
            var sketch = newSketch(context, id + "F16", { "sketchPlane" : qUnion([Q0])});
            skLineSegment(sketch, "E79", {"start": v(0, 90) * mm, "end": v(0, 120) * mm, "construction": true});
            skLineSegment(sketch, "E80", {"start": v(-33, 90) * mm, "end": v(-15, 108) * mm});
            skLineSegment(sketch, "E81", {"start": v(-15, 108) * mm, "end": v(-15, 120) * mm});
            skLineSegment(sketch, "E82", {"start": v(33, 90) * mm, "end": v(15, 108) * mm});
            skLineSegment(sketch, "E83", {"start": v(15, 108) * mm, "end": v(15, 120) * mm});
            skArc(sketch, "E84", {"start": v(15, 120) * mm, "mid": v(0, 135) * mm, "end": v(-15, 120) * mm});
            skCircle(sketch, "E85", {"center": v(0, 120) * mm, "radius": 6 * mm});
            skLineSegment(sketch, "E86", {"start": v(-80, 0) * mm, "end": v(80, 0) * mm, "construction": true});
            skLineSegment(sketch, "E87.MirrorCS", {"start": v(33, -90) * mm, "end": v(15, -108) * mm});
            skLineSegment(sketch, "E88.MirrorCS", {"start": v(-33, -90) * mm, "end": v(-15, -108) * mm});
            skLineSegment(sketch, "E89.MirrorCS", {"start": v(0, -90) * mm, "end": v(0, -120) * mm, "construction": true});
            skCircle(sketch, "E90.MirrorC", {"center": v(0, -120) * mm, "radius": 6 * mm});
            skLineSegment(sketch, "E91.MirrorCS", {"start": v(15, -108) * mm, "end": v(15, -120) * mm});
            skLineSegment(sketch, "E92.MirrorCS", {"start": v(-15, -108) * mm, "end": v(-15, -120) * mm});
            skArc(sketch, "E93.MirrorCS", {"start": v(15, -120) * mm, "mid": v(0, -135) * mm, "end": v(-15, -120) * mm});
            skSolve(sketch);
        }
        {
            var Q0;
            {var subQ1=sQuery(id+"F16.wireOp",EDGE,"E80");Q0=makeQuery(id+"F16.imprint","IMPRINT",FACE,{"disambiguationData":[TD([[makeQuery(id+"F16.imprint","IMPRINT",EDGE,{"derivedFrom":subQ1}),-1.0]])]});}
            var Q1;
            {var subQ1=sQuery(id+"F16.wireOp",EDGE,"E87.MirrorCS");Q1=makeQuery(id+"F16.imprint","IMPRINT",FACE,{"disambiguationData":[TD([[makeQuery(id+"F16.imprint","IMPRINT",EDGE,{"derivedFrom":subQ1}),-1.0]])]});}
            var Q2;
            Q2=makeQuery(id+"F16.imprint","IMPRINT",FACE,{"disambiguationData":[TD([[makeQuery(id+"F16.imprint","IMPRINT",EDGE,{"derivedFrom":makeQuery(id+"F1.opExtrude","CAP_EDGE",EDGE,{"disambiguationData":[OSD([sQuery(id+"F0.wireOp",EDGE,"E1.left")])],"isStart":true})}),-1.0]])]});
            var Q3;
            Q3=makeQuery(id+"F2.opExtrude","CAP_FACE",FACE,{"disambiguationData":[OSD([sQuery(id+"F0.wireOp",EDGE,"E12"),sQuery(id+"F0.wireOp",EDGE,"E13"),sQuery(id+"F0.wireOp",EDGE,"E14"),sQuery(id+"F0.wireOp",EDGE,"E15"),sQuery(id+"F0.wireOp",EDGE,"E17.filletArc"),sQuery(id+"F0.wireOp",EDGE,"E18.filletArc"),sQuery(id+"F0.wireOp",EDGE,"E19.filletArc"),sQuery(id+"F0.wireOp",EDGE,"E20.filletArc"),sQuery(id+"F0.wireOp",EDGE,"E25.0"),sQuery(id+"F0.wireOp",EDGE,"E25.1"),sQuery(id+"F0.wireOp",EDGE,"E25.2"),sQuery(id+"F0.wireOp",EDGE,"E25.3"),sQuery(id+"F0.wireOp",EDGE,"E25.4"),sQuery(id+"F0.wireOp",EDGE,"E25.5"),sQuery(id+"F0.wireOp",EDGE,"E25.6"),sQuery(id+"F0.wireOp",EDGE,"E25.7")])],"isStart":false});
            extrude(context, id + "F17", {"entities" : qUnion([Q0, Q1, Q2]), "endBound" : BoundingType.UP_TO_SURFACE, "depth" : 25 * mm, "endBoundEntityFace" : qUnion([Q3]), "offsetDistance" : 25 * mm});
        }
    });
